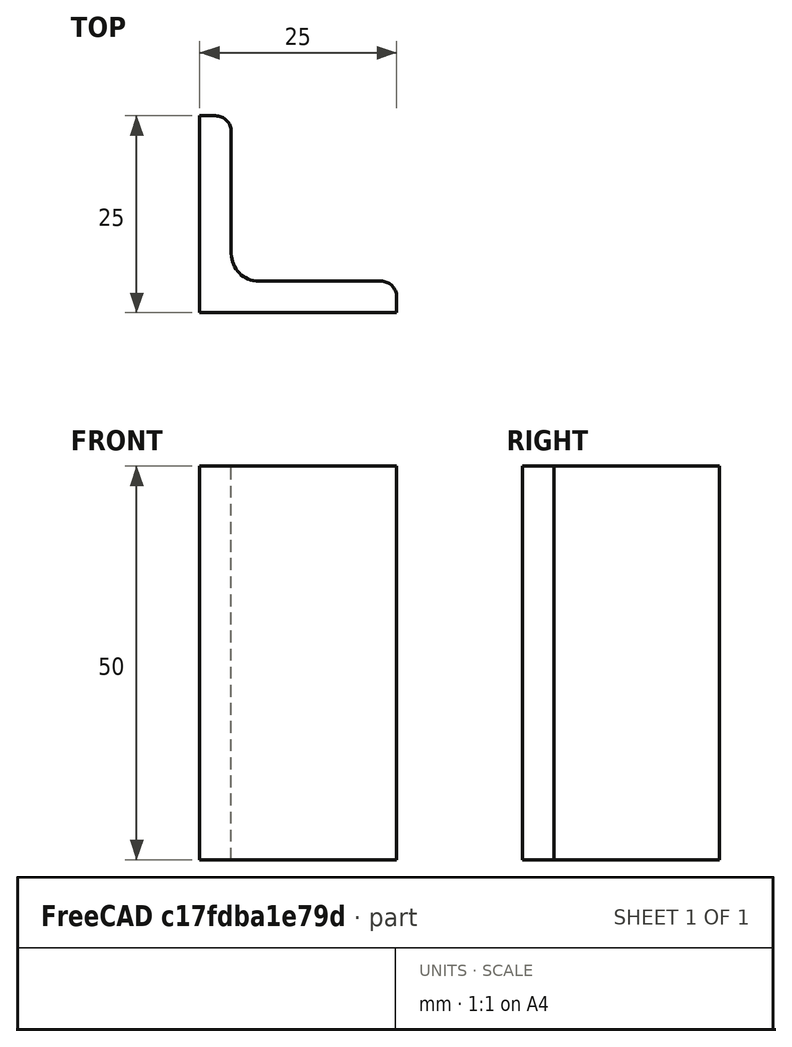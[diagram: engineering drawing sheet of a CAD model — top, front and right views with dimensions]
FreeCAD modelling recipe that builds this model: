
FCSTD DOCUMENT  (FreeCAD 0.15R4671 (Git))
Label: Angle Bar L25x25x4 EN10056 S235JR
License: All rights reserved
LicenseURL: http://en.wikipedia.org/wiki/All_rights_reserved
objects: Sketcher::SketchObject×1, Part::Extrusion×1
note: 2 computed .brp shape members not serialized (recipe doc carries the construction recipe); baked Part::Feature solids carry a one-line shape summary decoded from their .brp

FEATURE [Sketcher::SketchObject] Sketch
  sketch-geometry (9):
    g0: LineSegment StartX=0 StartY=0 StartZ=0 EndX=25 EndY=0 EndZ=0
    g1: LineSegment StartX=25 StartY=0 StartZ=0 EndX=25 EndY=2 EndZ=0
    g2: LineSegment StartX=23 StartY=4 StartZ=0 EndX=7.5 EndY=4 EndZ=0
    g3: LineSegment StartX=0 StartY=0 StartZ=0 EndX=0 EndY=25 EndZ=0
    g4: LineSegment StartX=0 StartY=25 StartZ=0 EndX=2 EndY=25 EndZ=0
    g5: LineSegment StartX=4 StartY=23 StartZ=0 EndX=4 EndY=7.5 EndZ=0
    g6: ArcOfCircle CenterX=7.5 CenterY=7.5 CenterZ=0 NormalX=0 NormalY=0 NormalZ=1 Radius=3.5 StartAngle=3.14159 EndAngle=4.71239
    g7: ArcOfCircle CenterX=2 CenterY=23 CenterZ=0 NormalX=0 NormalY=0 NormalZ=1 Radius=2 StartAngle=0 EndAngle=1.5708
    g8: ArcOfCircle CenterX=23 CenterY=2 CenterZ=0 NormalX=0 NormalY=0 NormalZ=1 Radius=2 StartAngle=0 EndAngle=1.5708
  constraints (23):
    c: Coincident(g0,g-1)
    c: Horizontal(g0)
    c: Coincident(g1,g0)
    c: Vertical(g1)
    c: Horizontal(g2)
    c: Coincident(g3,g-1)
    c: Vertical(g3)
    c: Coincident(g4,g3)
    c: Horizontal(g4)
    c: Vertical(g5)
    c: Tangent(g5,g6) = -1.5708
    c: Tangent(g2,g6) = 1.5708
    c: Tangent(g4,g7) = 1.5708
    c: Tangent(g5,g7) = 1.5708
    c: Tangent(g2,g8) = -1.5708
    c: Tangent(g1,g8) = -1.5708
    c: DistanceX(g0) = 25
    c: DistanceY(g3) = 25
    c: DistanceY(g0,g2) = 4
    c: DistanceX(g3,g5) = 4
    c: Radius(g6) = 3.5
    c: Radius(g8) = 2
    c: Radius(g7) = 2
FEATURE [Part::Extrusion] Extrude  label="Angle Bar L25x25x4 EN10056 S235JR"
  Base = -> Sketch
  Dir = (0,0,50)
  Solid = true
